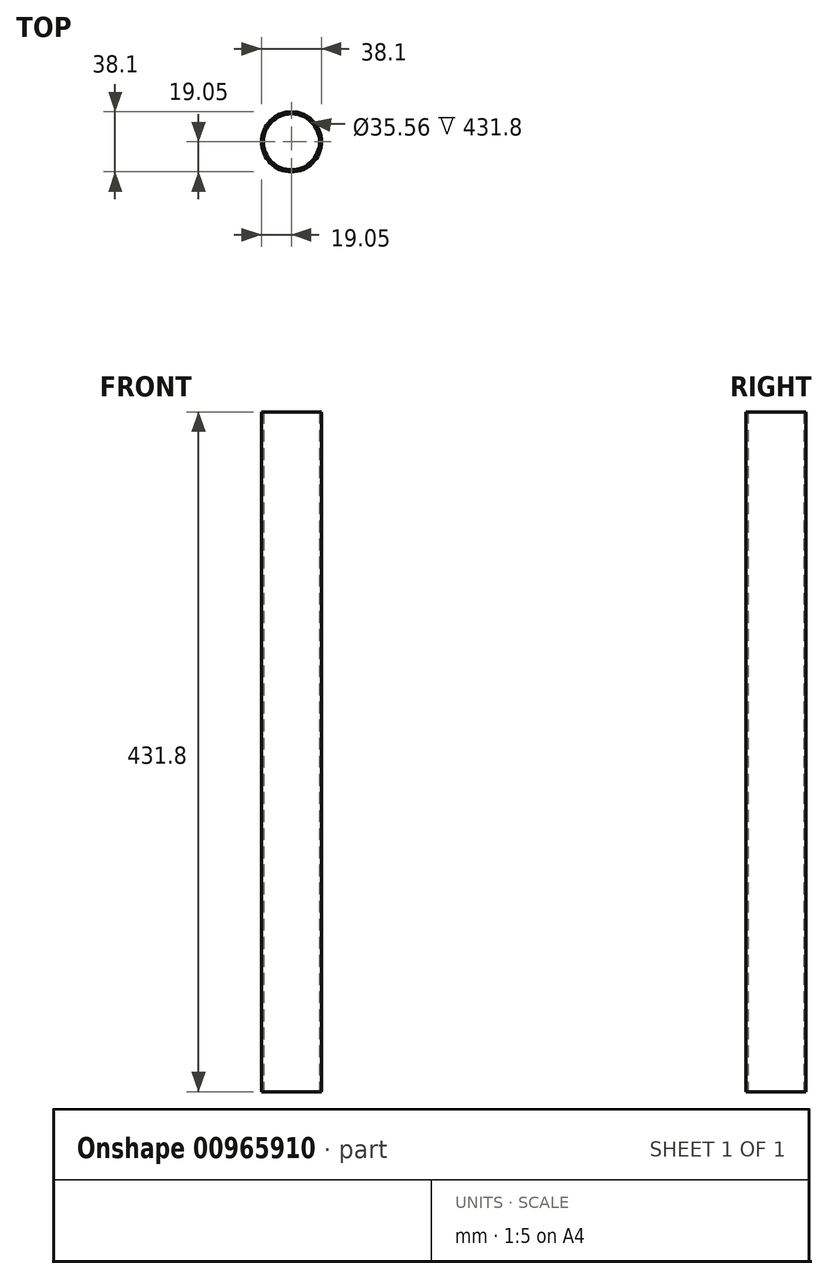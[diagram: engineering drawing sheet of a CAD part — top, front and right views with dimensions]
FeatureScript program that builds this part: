
annotation { "Feature Type Name" : "Feature", "Feature Type Description" : "" }
export const myFeature = defineFeature(function(context is Context, id is Id, definition is map)
    precondition{}
    {
        {
            var Q0;
            Q0=qCreatedBy(makeId("Top.planeOp"),FACE);
            var sketch = newSketch(context, id + "F0", { "sketchPlane" : qUnion([Q0])});
            skCircle(sketch, "E0", {"center": v(0, 0) * mm, "radius": 19.05 * mm});
            skCircle(sketch, "E1", {"center": v(0, 0) * mm, "radius": 17.78 * mm});
            skSolve(sketch);
        }
        {
            var Q0;
            Q0=makeQuery(id+"F0.imprint","IMPRINT",FACE,{"disambiguationData":[TD([[makeQuery(id+"F0.imprint","IMPRINT",EDGE,{"derivedFrom":sQuery(id+"F0.wireOp",EDGE,"E0")}),1.0]])]});
            extrude(context, id + "F1", {"entities" : qUnion([Q0]), "depth" : 431.8 * mm, "offsetDistance" : 25.4 * mm});
        }
    });
